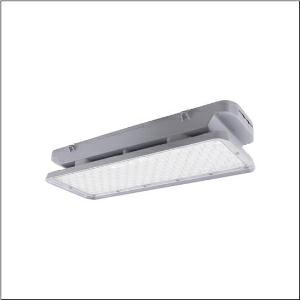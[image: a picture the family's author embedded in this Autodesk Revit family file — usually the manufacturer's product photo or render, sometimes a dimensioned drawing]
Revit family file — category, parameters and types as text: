
# Revit family: highbay_21-s_51hk42da4gca
name_source: partatom
category: Lighting Fixtures
units: mm (PartAtom-declared; Revit-internal decimal feet)

## family parameters
Cut with Voids When Loaded = No
Host = Face
Light Source = No
Part Type = Normal
Room Calculation Point = No
Round Connector Dimension = Use Diameter
Shared = No

## types (1)
- Highbay 21-S (1 x LED, 13500 lm, 75 W, 4000K)
    Apparent Load = 75 VA
    CIE Flux Codes = 74 96 100 100 100
    Color Rendering = 80
    Color Temperature = 4000K
    Default Elevation = 1800 mm
    Description = Highbay 21-S, LED high bay luminaire, primary light control with lens, of PC, light emission: direct distribution, primary light characteristic: symmetric, installation type: suspended mounting, surface-mounted, LED, rated luminous flux: 13.500lm, luminous efficacy: 179lm/W, light colour: 840, colour temperature: 4000K, with terminal, 5-pole, max. 2.5mm², mains connection: 220..240V, AC, 50Hz, rated input power: 75W, housing, of diecast aluminium, coated, grey, length: 471mm, width: 172mm, height: 87mm, protection rating (complete): IP66, insulation class (complete): insulation class I (protective earthing), certification: CE, ENEC, UKCA, protection symbol: D, impact resistance: IK08, permissible operating ambient temperature: -30..+60°C, corresponds to IFS (International Featured Standards) requirements for safety and quality in the food industry, LABS conformity tested according to VDMA 24364:2018-05, packaging unit: 1 piece
    Height = 89 mm
    Lamp = 1 x LED
    Lamp Light Flux = 13500 lm
    Lamp Power = 75 W
    Lamp count = 1
    Length = 471 mm
    Luminous efficacy = 180 lm/W
    Manufacturer = Siteco
    ModVariant = No
    Model = 51HK42DA4GCA
    Mounting Place = Ceiling
    Mounting Type = Pendant
    Number of Poles = 1
    OnlyDefault = Yes
    Power Factor = 1
    Product Name = Highbay 21-S
    Product group = LED high bay luminaire
    ProductGroupID = 903
    Protection Class = Protection class I
    Protection Degree = IP 66
    RLX_Detail_Level = 1
    RLX_Emergency_Light_Flux = 0 lm
    RLX_Emergency_Type = 0
    RLX_Emergency_Type_DB = No
    RlxData = <blob elided: 21961 chars, md5=10cf80ca>
    Socket = socket
    Standby Power = 0 W
    System Light Flux = 13500 lm
    System Power = 75 W
    Type Comments = Product without accessories
    Type Image = l_1276526.jpg
    URL = http://relux.com
    VarID = ---
    Voltage = 0 V
    Weight = 0.00 kg
    Width = 172 mm

## geometry (parser evidence)
native form markers: Blend x4, Sweep x11
no freeform markers — native parametric forms only
